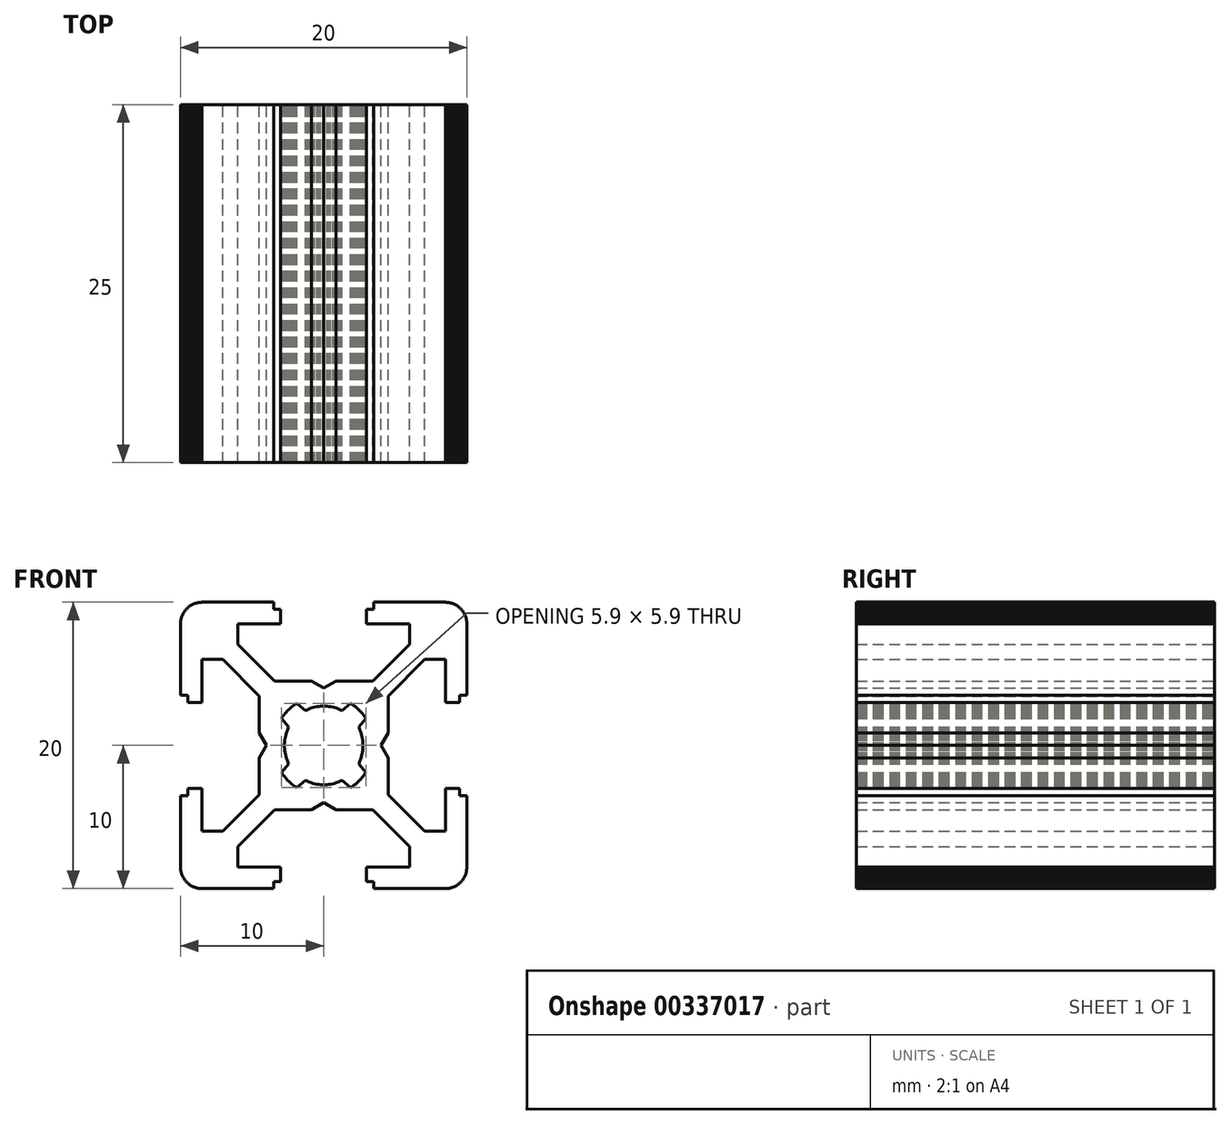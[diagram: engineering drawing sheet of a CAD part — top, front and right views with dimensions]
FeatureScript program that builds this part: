
annotation { "Feature Type Name" : "Feature", "Feature Type Description" : "" }
export const myFeature = defineFeature(function(context is Context, id is Id, definition is map)
    precondition{}
    {
        {
            var Q0;
            Q0=qCreatedBy(makeId("Front.planeOp"),FACE);
            var sketch = newSketch(context, id + "F0", { "sketchPlane" : qUnion([Q0])});
            skLineSegment(sketch, "E0", {"start": v(-10, -8.57) * mm, "end": v(-10, -8.5) * mm});
            skLineSegment(sketch, "E1", {"start": v(10, 8.5) * mm, "end": v(10, 8.57) * mm});
            skLineSegment(sketch, "E2", {"start": v(-2.74, -0.2) * mm, "end": v(-2.75, -0.07) * mm});
            skLineSegment(sketch, "E3", {"start": v(2.75, 0.07) * mm, "end": v(2.74, 0.2) * mm});
            skLineSegment(sketch, "E4", {"start": v(-10, -8.63) * mm, "end": v(-10, -8.57) * mm});
            skLineSegment(sketch, "E5", {"start": v(10, 8.57) * mm, "end": v(10, 8.63) * mm});
            skLineSegment(sketch, "E6", {"start": v(-2.73, -0.35) * mm, "end": v(-2.74, -0.2) * mm});
            skLineSegment(sketch, "E7", {"start": v(2.74, 0.2) * mm, "end": v(2.73, 0.35) * mm});
            skLineSegment(sketch, "E8", {"start": v(-9.99, -8.7) * mm, "end": v(-10, -8.63) * mm});
            skLineSegment(sketch, "E9", {"start": v(10, 8.63) * mm, "end": v(9.99, 8.7) * mm});
            skLineSegment(sketch, "E10", {"start": v(-2.7, -0.49) * mm, "end": v(-2.73, -0.35) * mm});
            skLineSegment(sketch, "E11", {"start": v(2.73, 0.35) * mm, "end": v(2.7, 0.49) * mm});
            skLineSegment(sketch, "E12", {"start": v(-9.98, -8.77) * mm, "end": v(-9.99, -8.7) * mm});
            skLineSegment(sketch, "E13", {"start": v(9.99, 8.7) * mm, "end": v(9.98, 8.77) * mm});
            skLineSegment(sketch, "E14", {"start": v(-9.96, -8.83) * mm, "end": v(-9.98, -8.77) * mm});
            skLineSegment(sketch, "E15", {"start": v(9.98, 8.77) * mm, "end": v(9.96, 8.83) * mm});
            skLineSegment(sketch, "E16", {"start": v(-2.68, -0.62) * mm, "end": v(-2.7, -0.49) * mm});
            skLineSegment(sketch, "E17", {"start": v(2.7, 0.49) * mm, "end": v(2.68, 0.62) * mm});
            skLineSegment(sketch, "E18", {"start": v(-9.95, -8.9) * mm, "end": v(-9.96, -8.83) * mm});
            skLineSegment(sketch, "E19", {"start": v(9.96, 8.83) * mm, "end": v(9.95, 8.9) * mm});
            skLineSegment(sketch, "E20", {"start": v(-2.64, -0.76) * mm, "end": v(-2.68, -0.62) * mm});
            skLineSegment(sketch, "E21", {"start": v(2.68, 0.62) * mm, "end": v(2.64, 0.76) * mm});
            skLineSegment(sketch, "E22", {"start": v(-9.93, -8.96) * mm, "end": v(-9.95, -8.9) * mm});
            skLineSegment(sketch, "E23", {"start": v(9.95, 8.9) * mm, "end": v(9.93, 8.96) * mm});
            skLineSegment(sketch, "E24", {"start": v(-2.6, -0.9) * mm, "end": v(-2.64, -0.76) * mm});
            skLineSegment(sketch, "E25", {"start": v(2.64, 0.76) * mm, "end": v(2.6, 0.9) * mm});
            skLineSegment(sketch, "E26", {"start": v(-9.9, -9.03) * mm, "end": v(-9.93, -8.96) * mm});
            skLineSegment(sketch, "E27", {"start": v(9.93, 8.96) * mm, "end": v(9.9, 9.03) * mm});
            skLineSegment(sketch, "E28", {"start": v(-2.55, -1.02) * mm, "end": v(-2.6, -0.9) * mm});
            skLineSegment(sketch, "E29", {"start": v(2.6, 0.9) * mm, "end": v(2.55, 1.02) * mm});
            skLineSegment(sketch, "E30", {"start": v(-9.88, -9.09) * mm, "end": v(-9.9, -9.03) * mm});
            skLineSegment(sketch, "E31", {"start": v(9.9, 9.03) * mm, "end": v(9.88, 9.09) * mm});
            skLineSegment(sketch, "E32", {"start": v(-2.5, -1.15) * mm, "end": v(-2.55, -1.02) * mm});
            skLineSegment(sketch, "E33", {"start": v(2.55, 1.02) * mm, "end": v(2.5, 1.15) * mm});
            skLineSegment(sketch, "E34", {"start": v(-9.85, -9.15) * mm, "end": v(-9.88, -9.09) * mm});
            skLineSegment(sketch, "E35", {"start": v(9.88, 9.09) * mm, "end": v(9.85, 9.15) * mm});
            skLineSegment(sketch, "E36", {"start": v(-2.44, -1.28) * mm, "end": v(-2.5, -1.15) * mm});
            skLineSegment(sketch, "E37", {"start": v(2.5, 1.15) * mm, "end": v(2.44, 1.28) * mm});
            skLineSegment(sketch, "E38", {"start": v(-9.82, -9.21) * mm, "end": v(-9.85, -9.15) * mm});
            skLineSegment(sketch, "E39", {"start": v(9.85, 9.15) * mm, "end": v(9.82, 9.21) * mm});
            skLineSegment(sketch, "E40", {"start": v(-9.79, -9.27) * mm, "end": v(-9.82, -9.21) * mm});
            skLineSegment(sketch, "E41", {"start": v(9.82, 9.21) * mm, "end": v(9.79, 9.27) * mm});
            skLineSegment(sketch, "E42", {"start": v(4.5, -0.87) * mm, "end": v(4, 0) * mm});
            skLineSegment(sketch, "E43", {"start": v(-4, 0) * mm, "end": v(-4.5, 0.87) * mm});
            skLineSegment(sketch, "E44", {"start": v(-9.75, -9.33) * mm, "end": v(-9.79, -9.27) * mm});
            skLineSegment(sketch, "E45", {"start": v(9.79, 9.27) * mm, "end": v(9.75, 9.33) * mm});
            skLineSegment(sketch, "E46", {"start": v(-2.87, -2) * mm, "end": v(-2.95, -1.89) * mm});
            skLineSegment(sketch, "E47", {"start": v(2.95, 1.89) * mm, "end": v(2.87, 2) * mm});
            skLineSegment(sketch, "E48", {"start": v(-9.71, -9.38) * mm, "end": v(-9.75, -9.33) * mm});
            skLineSegment(sketch, "E49", {"start": v(9.75, 9.33) * mm, "end": v(9.71, 9.38) * mm});
            skLineSegment(sketch, "E50", {"start": v(-2.8, -2.11) * mm, "end": v(-2.87, -2) * mm});
            skLineSegment(sketch, "E51", {"start": v(2.87, 2) * mm, "end": v(2.8, 2.11) * mm});
            skLineSegment(sketch, "E52", {"start": v(-9.67, -9.44) * mm, "end": v(-9.71, -9.38) * mm});
            skLineSegment(sketch, "E53", {"start": v(9.71, 9.38) * mm, "end": v(9.67, 9.44) * mm});
            skLineSegment(sketch, "E54", {"start": v(-2.7, -2.22) * mm, "end": v(-2.8, -2.11) * mm});
            skLineSegment(sketch, "E55", {"start": v(2.8, 2.11) * mm, "end": v(2.7, 2.22) * mm});
            skLineSegment(sketch, "E56", {"start": v(-9.63, -9.49) * mm, "end": v(-9.67, -9.44) * mm});
            skLineSegment(sketch, "E57", {"start": v(9.67, 9.44) * mm, "end": v(9.63, 9.49) * mm});
            skLineSegment(sketch, "E58", {"start": v(2.95, -1.89) * mm, "end": v(2.44, -1.28) * mm});
            skLineSegment(sketch, "E59", {"start": v(-2.44, 1.28) * mm, "end": v(-2.95, 1.89) * mm});
            skLineSegment(sketch, "E60", {"start": v(-2.62, -2.32) * mm, "end": v(-2.7, -2.22) * mm});
            skLineSegment(sketch, "E61", {"start": v(2.7, 2.22) * mm, "end": v(2.62, 2.32) * mm});
            skLineSegment(sketch, "E62", {"start": v(-9.58, -9.54) * mm, "end": v(-9.63, -9.49) * mm});
            skLineSegment(sketch, "E63", {"start": v(9.63, 9.49) * mm, "end": v(9.58, 9.54) * mm});
            skLineSegment(sketch, "E64", {"start": v(-2.52, -2.43) * mm, "end": v(-2.62, -2.32) * mm});
            skLineSegment(sketch, "E65", {"start": v(2.62, 2.32) * mm, "end": v(2.52, 2.43) * mm});
            skLineSegment(sketch, "E66", {"start": v(-2.43, -2.52) * mm, "end": v(-2.52, -2.43) * mm});
            skLineSegment(sketch, "E67", {"start": v(2.52, 2.43) * mm, "end": v(2.43, 2.52) * mm});
            skLineSegment(sketch, "E68", {"start": v(-9.54, -9.58) * mm, "end": v(-9.58, -9.54) * mm});
            skLineSegment(sketch, "E69", {"start": v(7.06, -6) * mm, "end": v(4.5, -3.44) * mm});
            skLineSegment(sketch, "E70", {"start": v(-4.5, 3.44) * mm, "end": v(-7.06, 6) * mm});
            skLineSegment(sketch, "E71", {"start": v(6, -7.06) * mm, "end": v(3.44, -4.5) * mm});
            skLineSegment(sketch, "E72", {"start": v(-3.44, 4.5) * mm, "end": v(-6, 7.06) * mm});
            skLineSegment(sketch, "E73", {"start": v(9.58, 9.54) * mm, "end": v(9.54, 9.58) * mm});
            skLineSegment(sketch, "E74", {"start": v(-2.32, -2.62) * mm, "end": v(-2.43, -2.52) * mm});
            skLineSegment(sketch, "E75", {"start": v(2.43, 2.52) * mm, "end": v(2.32, 2.62) * mm});
            skLineSegment(sketch, "E76", {"start": v(-9.49, -9.63) * mm, "end": v(-9.54, -9.58) * mm});
            skLineSegment(sketch, "E77", {"start": v(9.54, 9.58) * mm, "end": v(9.49, 9.63) * mm});
            skLineSegment(sketch, "E78", {"start": v(-2.22, -2.7) * mm, "end": v(-2.32, -2.62) * mm});
            skLineSegment(sketch, "E79", {"start": v(2.32, 2.62) * mm, "end": v(2.22, 2.7) * mm});
            skLineSegment(sketch, "E80", {"start": v(1.89, -2.95) * mm, "end": v(1.28, -2.44) * mm});
            skLineSegment(sketch, "E81", {"start": v(-1.28, 2.44) * mm, "end": v(-1.89, 2.95) * mm});
            skLineSegment(sketch, "E82", {"start": v(-9.44, -9.67) * mm, "end": v(-9.49, -9.63) * mm});
            skLineSegment(sketch, "E83", {"start": v(9.49, 9.63) * mm, "end": v(9.44, 9.67) * mm});
            skLineSegment(sketch, "E84", {"start": v(-2.11, -2.8) * mm, "end": v(-2.22, -2.7) * mm});
            skLineSegment(sketch, "E85", {"start": v(2.22, 2.7) * mm, "end": v(2.11, 2.8) * mm});
            skLineSegment(sketch, "E86", {"start": v(-9.38, -9.71) * mm, "end": v(-9.44, -9.67) * mm});
            skLineSegment(sketch, "E87", {"start": v(9.44, 9.67) * mm, "end": v(9.38, 9.71) * mm});
            skLineSegment(sketch, "E88", {"start": v(-2, -2.87) * mm, "end": v(-2.11, -2.8) * mm});
            skLineSegment(sketch, "E89", {"start": v(2.11, 2.8) * mm, "end": v(2, 2.87) * mm});
            skLineSegment(sketch, "E90", {"start": v(-9.33, -9.75) * mm, "end": v(-9.38, -9.71) * mm});
            skLineSegment(sketch, "E91", {"start": v(9.38, 9.71) * mm, "end": v(9.33, 9.75) * mm});
            skLineSegment(sketch, "E92", {"start": v(-1.89, -2.95) * mm, "end": v(-2, -2.87) * mm});
            skLineSegment(sketch, "E93", {"start": v(2, 2.87) * mm, "end": v(1.89, 2.95) * mm});
            skLineSegment(sketch, "E94", {"start": v(-9.27, -9.79) * mm, "end": v(-9.33, -9.75) * mm});
            skLineSegment(sketch, "E95", {"start": v(9.33, 9.75) * mm, "end": v(9.27, 9.79) * mm});
            skLineSegment(sketch, "E96", {"start": v(0.87, -4.5) * mm, "end": v(0, -4) * mm});
            skLineSegment(sketch, "E97", {"start": v(0, 4) * mm, "end": v(-0.87, 4.5) * mm});
            skLineSegment(sketch, "E98", {"start": v(-9.21, -9.82) * mm, "end": v(-9.27, -9.79) * mm});
            skLineSegment(sketch, "E99", {"start": v(9.27, 9.79) * mm, "end": v(9.21, 9.82) * mm});
            skLineSegment(sketch, "E100", {"start": v(-9.15, -9.85) * mm, "end": v(-9.21, -9.82) * mm});
            skLineSegment(sketch, "E101", {"start": v(9.21, 9.82) * mm, "end": v(9.15, 9.85) * mm});
            skLineSegment(sketch, "E102", {"start": v(-1.15, -2.5) * mm, "end": v(-1.28, -2.44) * mm});
            skLineSegment(sketch, "E103", {"start": v(1.28, 2.44) * mm, "end": v(1.15, 2.5) * mm});
            skLineSegment(sketch, "E104", {"start": v(-9.09, -9.88) * mm, "end": v(-9.15, -9.85) * mm});
            skLineSegment(sketch, "E105", {"start": v(9.15, 9.85) * mm, "end": v(9.09, 9.88) * mm});
            skLineSegment(sketch, "E106", {"start": v(-1.02, -2.55) * mm, "end": v(-1.15, -2.5) * mm});
            skLineSegment(sketch, "E107", {"start": v(1.15, 2.5) * mm, "end": v(1.02, 2.55) * mm});
            skLineSegment(sketch, "E108", {"start": v(-9.03, -9.9) * mm, "end": v(-9.09, -9.88) * mm});
            skLineSegment(sketch, "E109", {"start": v(9.09, 9.88) * mm, "end": v(9.03, 9.9) * mm});
            skLineSegment(sketch, "E110", {"start": v(-0.9, -2.6) * mm, "end": v(-1.02, -2.55) * mm});
            skLineSegment(sketch, "E111", {"start": v(1.02, 2.55) * mm, "end": v(0.9, 2.6) * mm});
            skLineSegment(sketch, "E112", {"start": v(-8.96, -9.93) * mm, "end": v(-9.03, -9.9) * mm});
            skLineSegment(sketch, "E113", {"start": v(9.03, 9.9) * mm, "end": v(8.96, 9.93) * mm});
            skLineSegment(sketch, "E114", {"start": v(-0.76, -2.64) * mm, "end": v(-0.9, -2.6) * mm});
            skLineSegment(sketch, "E115", {"start": v(0.9, 2.6) * mm, "end": v(0.76, 2.64) * mm});
            skLineSegment(sketch, "E116", {"start": v(-8.9, -9.95) * mm, "end": v(-8.96, -9.93) * mm});
            skLineSegment(sketch, "E117", {"start": v(8.96, 9.93) * mm, "end": v(8.9, 9.95) * mm});
            skLineSegment(sketch, "E118", {"start": v(-0.62, -2.68) * mm, "end": v(-0.76, -2.64) * mm});
            skLineSegment(sketch, "E119", {"start": v(0.76, 2.64) * mm, "end": v(0.62, 2.68) * mm});
            skLineSegment(sketch, "E120", {"start": v(-8.83, -9.96) * mm, "end": v(-8.9, -9.95) * mm});
            skLineSegment(sketch, "E121", {"start": v(8.9, 9.95) * mm, "end": v(8.83, 9.96) * mm});
            skLineSegment(sketch, "E122", {"start": v(-0.49, -2.7) * mm, "end": v(-0.62, -2.68) * mm});
            skLineSegment(sketch, "E123", {"start": v(0.62, 2.68) * mm, "end": v(0.49, 2.7) * mm});
            skLineSegment(sketch, "E124", {"start": v(-8.77, -9.98) * mm, "end": v(-8.83, -9.96) * mm});
            skLineSegment(sketch, "E125", {"start": v(8.83, 9.96) * mm, "end": v(8.77, 9.98) * mm});
            skLineSegment(sketch, "E126", {"start": v(-8.7, -9.99) * mm, "end": v(-8.77, -9.98) * mm});
            skLineSegment(sketch, "E127", {"start": v(8.77, 9.98) * mm, "end": v(8.7, 9.99) * mm});
            skLineSegment(sketch, "E128", {"start": v(-0.35, -2.73) * mm, "end": v(-0.49, -2.7) * mm});
            skLineSegment(sketch, "E129", {"start": v(0.49, 2.7) * mm, "end": v(0.35, 2.73) * mm});
            skLineSegment(sketch, "E130", {"start": v(-8.63, -10) * mm, "end": v(-8.7, -9.99) * mm});
            skLineSegment(sketch, "E131", {"start": v(8.7, 9.99) * mm, "end": v(8.63, 10) * mm});
            skLineSegment(sketch, "E132", {"start": v(-0.2, -2.74) * mm, "end": v(-0.35, -2.73) * mm});
            skLineSegment(sketch, "E133", {"start": v(0.35, 2.73) * mm, "end": v(0.2, 2.74) * mm});
            skLineSegment(sketch, "E134", {"start": v(-8.57, -10) * mm, "end": v(-8.63, -10) * mm});
            skLineSegment(sketch, "E135", {"start": v(8.63, 10) * mm, "end": v(8.57, 10) * mm});
            skLineSegment(sketch, "E136", {"start": v(-0.07, -2.75) * mm, "end": v(-0.2, -2.74) * mm});
            skLineSegment(sketch, "E137", {"start": v(0.2, 2.74) * mm, "end": v(0.07, 2.75) * mm});
            skLineSegment(sketch, "E138", {"start": v(-8.5, -10) * mm, "end": v(-8.57, -10) * mm});
            skLineSegment(sketch, "E139", {"start": v(8.57, 10) * mm, "end": v(8.5, 10) * mm});
            skLineSegment(sketch, "E140", {"start": v(-8.5, -10) * mm, "end": v(-3.5, -10) * mm});
            skLineSegment(sketch, "E141", {"start": v(3.5, -10) * mm, "end": v(8.5, -10) * mm});
            skLineSegment(sketch, "E142", {"start": v(-3.5, -9.5) * mm, "end": v(-3, -9.5) * mm});
            skLineSegment(sketch, "E143", {"start": v(3, -9.5) * mm, "end": v(3.5, -9.5) * mm});
            skLineSegment(sketch, "E144", {"start": v(-6, -8.5) * mm, "end": v(-3, -8.5) * mm});
            skLineSegment(sketch, "E145", {"start": v(3, -8.5) * mm, "end": v(6, -8.5) * mm});
            skLineSegment(sketch, "E146", {"start": v(-8.5, -6) * mm, "end": v(-7.06, -6) * mm});
            skLineSegment(sketch, "E147", {"start": v(7.06, -6) * mm, "end": v(8.5, -6) * mm});
            skLineSegment(sketch, "E148", {"start": v(-3.44, -4.5) * mm, "end": v(-0.87, -4.5) * mm});
            skLineSegment(sketch, "E149", {"start": v(0.87, -4.5) * mm, "end": v(3.44, -4.5) * mm});
            skLineSegment(sketch, "E150", {"start": v(-10, -3.5) * mm, "end": v(-9.5, -3.5) * mm});
            skLineSegment(sketch, "E151", {"start": v(9.5, -3.5) * mm, "end": v(10, -3.5) * mm});
            skLineSegment(sketch, "E152", {"start": v(-9.5, -3) * mm, "end": v(-8.5, -3) * mm});
            skLineSegment(sketch, "E153", {"start": v(8.5, -3) * mm, "end": v(9.5, -3) * mm});
            skLineSegment(sketch, "E154", {"start": v(-0.07, -2.75) * mm, "end": v(0.07, -2.75) * mm});
            skLineSegment(sketch, "E155", {"start": v(-0.07, 2.75) * mm, "end": v(0.07, 2.75) * mm});
            skLineSegment(sketch, "E156", {"start": v(8.5, 3) * mm, "end": v(9.5, 3) * mm});
            skLineSegment(sketch, "E157", {"start": v(-9.5, 3) * mm, "end": v(-8.5, 3) * mm});
            skLineSegment(sketch, "E158", {"start": v(9.5, 3.5) * mm, "end": v(10, 3.5) * mm});
            skLineSegment(sketch, "E159", {"start": v(-10, 3.5) * mm, "end": v(-9.5, 3.5) * mm});
            skLineSegment(sketch, "E160", {"start": v(0.87, 4.5) * mm, "end": v(3.44, 4.5) * mm});
            skLineSegment(sketch, "E161", {"start": v(-3.44, 4.5) * mm, "end": v(-0.87, 4.5) * mm});
            skLineSegment(sketch, "E162", {"start": v(7.06, 6) * mm, "end": v(8.5, 6) * mm});
            skLineSegment(sketch, "E163", {"start": v(-8.5, 6) * mm, "end": v(-7.06, 6) * mm});
            skLineSegment(sketch, "E164", {"start": v(3, 8.5) * mm, "end": v(6, 8.5) * mm});
            skLineSegment(sketch, "E165", {"start": v(-6, 8.5) * mm, "end": v(-3, 8.5) * mm});
            skLineSegment(sketch, "E166", {"start": v(3, 9.5) * mm, "end": v(3.5, 9.5) * mm});
            skLineSegment(sketch, "E167", {"start": v(-3.5, 9.5) * mm, "end": v(-3, 9.5) * mm});
            skLineSegment(sketch, "E168", {"start": v(3.5, 10) * mm, "end": v(8.5, 10) * mm});
            skLineSegment(sketch, "E169", {"start": v(-8.5, 10) * mm, "end": v(-3.5, 10) * mm});
            skLineSegment(sketch, "E170", {"start": v(8.5, -10) * mm, "end": v(8.57, -10) * mm});
            skLineSegment(sketch, "E171", {"start": v(-8.57, 10) * mm, "end": v(-8.5, 10) * mm});
            skLineSegment(sketch, "E172", {"start": v(0.07, -2.75) * mm, "end": v(0.2, -2.74) * mm});
            skLineSegment(sketch, "E173", {"start": v(-0.2, 2.74) * mm, "end": v(-0.07, 2.75) * mm});
            skLineSegment(sketch, "E174", {"start": v(8.57, -10) * mm, "end": v(8.63, -10) * mm});
            skLineSegment(sketch, "E175", {"start": v(-8.63, 10) * mm, "end": v(-8.57, 10) * mm});
            skLineSegment(sketch, "E176", {"start": v(0.2, -2.74) * mm, "end": v(0.35, -2.73) * mm});
            skLineSegment(sketch, "E177", {"start": v(-0.35, 2.73) * mm, "end": v(-0.2, 2.74) * mm});
            skLineSegment(sketch, "E178", {"start": v(8.63, -10) * mm, "end": v(8.7, -9.99) * mm});
            skLineSegment(sketch, "E179", {"start": v(-8.7, 9.99) * mm, "end": v(-8.63, 10) * mm});
            skLineSegment(sketch, "E180", {"start": v(0.35, -2.73) * mm, "end": v(0.49, -2.7) * mm});
            skLineSegment(sketch, "E181", {"start": v(-0.49, 2.7) * mm, "end": v(-0.35, 2.73) * mm});
            skLineSegment(sketch, "E182", {"start": v(8.7, -9.99) * mm, "end": v(8.77, -9.98) * mm});
            skLineSegment(sketch, "E183", {"start": v(-8.77, 9.98) * mm, "end": v(-8.7, 9.99) * mm});
            skLineSegment(sketch, "E184", {"start": v(8.77, -9.98) * mm, "end": v(8.83, -9.96) * mm});
            skLineSegment(sketch, "E185", {"start": v(-8.83, 9.96) * mm, "end": v(-8.77, 9.98) * mm});
            skLineSegment(sketch, "E186", {"start": v(0.49, -2.7) * mm, "end": v(0.62, -2.68) * mm});
            skLineSegment(sketch, "E187", {"start": v(-0.62, 2.68) * mm, "end": v(-0.49, 2.7) * mm});
            skLineSegment(sketch, "E188", {"start": v(8.83, -9.96) * mm, "end": v(8.9, -9.95) * mm});
            skLineSegment(sketch, "E189", {"start": v(-8.9, 9.95) * mm, "end": v(-8.83, 9.96) * mm});
            skLineSegment(sketch, "E190", {"start": v(0.62, -2.68) * mm, "end": v(0.76, -2.64) * mm});
            skLineSegment(sketch, "E191", {"start": v(-0.76, 2.64) * mm, "end": v(-0.62, 2.68) * mm});
            skLineSegment(sketch, "E192", {"start": v(8.9, -9.95) * mm, "end": v(8.96, -9.93) * mm});
            skLineSegment(sketch, "E193", {"start": v(-8.96, 9.93) * mm, "end": v(-8.9, 9.95) * mm});
            skLineSegment(sketch, "E194", {"start": v(0.76, -2.64) * mm, "end": v(0.9, -2.6) * mm});
            skLineSegment(sketch, "E195", {"start": v(-0.9, 2.6) * mm, "end": v(-0.76, 2.64) * mm});
            skLineSegment(sketch, "E196", {"start": v(8.96, -9.93) * mm, "end": v(9.03, -9.9) * mm});
            skLineSegment(sketch, "E197", {"start": v(-9.03, 9.9) * mm, "end": v(-8.96, 9.93) * mm});
            skLineSegment(sketch, "E198", {"start": v(0.9, -2.6) * mm, "end": v(1.02, -2.55) * mm});
            skLineSegment(sketch, "E199", {"start": v(-1.02, 2.55) * mm, "end": v(-0.9, 2.6) * mm});
            skLineSegment(sketch, "E200", {"start": v(9.03, -9.9) * mm, "end": v(9.09, -9.88) * mm});
            skLineSegment(sketch, "E201", {"start": v(-9.09, 9.88) * mm, "end": v(-9.03, 9.9) * mm});
            skLineSegment(sketch, "E202", {"start": v(1.02, -2.55) * mm, "end": v(1.15, -2.5) * mm});
            skLineSegment(sketch, "E203", {"start": v(-1.15, 2.5) * mm, "end": v(-1.02, 2.55) * mm});
            skLineSegment(sketch, "E204", {"start": v(9.09, -9.88) * mm, "end": v(9.15, -9.85) * mm});
            skLineSegment(sketch, "E205", {"start": v(-9.15, 9.85) * mm, "end": v(-9.09, 9.88) * mm});
            skLineSegment(sketch, "E206", {"start": v(1.15, -2.5) * mm, "end": v(1.28, -2.44) * mm});
            skLineSegment(sketch, "E207", {"start": v(-1.28, 2.44) * mm, "end": v(-1.15, 2.5) * mm});
            skLineSegment(sketch, "E208", {"start": v(9.15, -9.85) * mm, "end": v(9.21, -9.82) * mm});
            skLineSegment(sketch, "E209", {"start": v(-9.21, 9.82) * mm, "end": v(-9.15, 9.85) * mm});
            skLineSegment(sketch, "E210", {"start": v(9.21, -9.82) * mm, "end": v(9.27, -9.79) * mm});
            skLineSegment(sketch, "E211", {"start": v(-9.27, 9.79) * mm, "end": v(-9.21, 9.82) * mm});
            skLineSegment(sketch, "E212", {"start": v(-0.87, -4.5) * mm, "end": v(0, -4) * mm});
            skLineSegment(sketch, "E213", {"start": v(0, 4) * mm, "end": v(0.87, 4.5) * mm});
            skLineSegment(sketch, "E214", {"start": v(9.27, -9.79) * mm, "end": v(9.33, -9.75) * mm});
            skLineSegment(sketch, "E215", {"start": v(-9.33, 9.75) * mm, "end": v(-9.27, 9.79) * mm});
            skLineSegment(sketch, "E216", {"start": v(1.89, -2.95) * mm, "end": v(2, -2.87) * mm});
            skLineSegment(sketch, "E217", {"start": v(-2, 2.87) * mm, "end": v(-1.89, 2.95) * mm});
            skLineSegment(sketch, "E218", {"start": v(9.33, -9.75) * mm, "end": v(9.38, -9.71) * mm});
            skLineSegment(sketch, "E219", {"start": v(-9.38, 9.71) * mm, "end": v(-9.33, 9.75) * mm});
            skLineSegment(sketch, "E220", {"start": v(2, -2.87) * mm, "end": v(2.11, -2.8) * mm});
            skLineSegment(sketch, "E221", {"start": v(-2.11, 2.8) * mm, "end": v(-2, 2.87) * mm});
            skLineSegment(sketch, "E222", {"start": v(9.38, -9.71) * mm, "end": v(9.44, -9.67) * mm});
            skLineSegment(sketch, "E223", {"start": v(-9.44, 9.67) * mm, "end": v(-9.38, 9.71) * mm});
            skLineSegment(sketch, "E224", {"start": v(2.11, -2.8) * mm, "end": v(2.22, -2.7) * mm});
            skLineSegment(sketch, "E225", {"start": v(-2.22, 2.7) * mm, "end": v(-2.11, 2.8) * mm});
            skLineSegment(sketch, "E226", {"start": v(9.44, -9.67) * mm, "end": v(9.49, -9.63) * mm});
            skLineSegment(sketch, "E227", {"start": v(-9.49, 9.63) * mm, "end": v(-9.44, 9.67) * mm});
            skLineSegment(sketch, "E228", {"start": v(-1.89, -2.95) * mm, "end": v(-1.28, -2.44) * mm});
            skLineSegment(sketch, "E229", {"start": v(1.28, 2.44) * mm, "end": v(1.89, 2.95) * mm});
            skLineSegment(sketch, "E230", {"start": v(2.22, -2.7) * mm, "end": v(2.32, -2.62) * mm});
            skLineSegment(sketch, "E231", {"start": v(-2.32, 2.62) * mm, "end": v(-2.22, 2.7) * mm});
            skLineSegment(sketch, "E232", {"start": v(9.49, -9.63) * mm, "end": v(9.54, -9.58) * mm});
            skLineSegment(sketch, "E233", {"start": v(-9.54, 9.58) * mm, "end": v(-9.49, 9.63) * mm});
            skLineSegment(sketch, "E234", {"start": v(2.32, -2.62) * mm, "end": v(2.43, -2.52) * mm});
            skLineSegment(sketch, "E235", {"start": v(-2.43, 2.52) * mm, "end": v(-2.32, 2.62) * mm});
            skLineSegment(sketch, "E236", {"start": v(9.54, -9.58) * mm, "end": v(9.58, -9.54) * mm});
            skLineSegment(sketch, "E237", {"start": v(-7.06, -6) * mm, "end": v(-4.5, -3.44) * mm});
            skLineSegment(sketch, "E238", {"start": v(4.5, 3.44) * mm, "end": v(7.06, 6) * mm});
            skLineSegment(sketch, "E239", {"start": v(-6, -7.06) * mm, "end": v(-3.44, -4.5) * mm});
            skLineSegment(sketch, "E240", {"start": v(3.44, 4.5) * mm, "end": v(6, 7.06) * mm});
            skLineSegment(sketch, "E241", {"start": v(-9.58, 9.54) * mm, "end": v(-9.54, 9.58) * mm});
            skLineSegment(sketch, "E242", {"start": v(2.43, -2.52) * mm, "end": v(2.52, -2.43) * mm});
            skLineSegment(sketch, "E243", {"start": v(-2.52, 2.43) * mm, "end": v(-2.43, 2.52) * mm});
            skLineSegment(sketch, "E244", {"start": v(2.52, -2.43) * mm, "end": v(2.62, -2.32) * mm});
            skLineSegment(sketch, "E245", {"start": v(-2.62, 2.32) * mm, "end": v(-2.52, 2.43) * mm});
            skLineSegment(sketch, "E246", {"start": v(9.58, -9.54) * mm, "end": v(9.63, -9.49) * mm});
            skLineSegment(sketch, "E247", {"start": v(-9.63, 9.49) * mm, "end": v(-9.58, 9.54) * mm});
            skLineSegment(sketch, "E248", {"start": v(2.62, -2.32) * mm, "end": v(2.7, -2.22) * mm});
            skLineSegment(sketch, "E249", {"start": v(-2.7, 2.22) * mm, "end": v(-2.62, 2.32) * mm});
            skLineSegment(sketch, "E250", {"start": v(-2.95, -1.89) * mm, "end": v(-2.44, -1.28) * mm});
            skLineSegment(sketch, "E251", {"start": v(2.44, 1.28) * mm, "end": v(2.95, 1.89) * mm});
            skLineSegment(sketch, "E252", {"start": v(9.63, -9.49) * mm, "end": v(9.67, -9.44) * mm});
            skLineSegment(sketch, "E253", {"start": v(-9.67, 9.44) * mm, "end": v(-9.63, 9.49) * mm});
            skLineSegment(sketch, "E254", {"start": v(2.7, -2.22) * mm, "end": v(2.8, -2.11) * mm});
            skLineSegment(sketch, "E255", {"start": v(-2.8, 2.11) * mm, "end": v(-2.7, 2.22) * mm});
            skLineSegment(sketch, "E256", {"start": v(9.67, -9.44) * mm, "end": v(9.71, -9.38) * mm});
            skLineSegment(sketch, "E257", {"start": v(-9.71, 9.38) * mm, "end": v(-9.67, 9.44) * mm});
            skLineSegment(sketch, "E258", {"start": v(2.8, -2.11) * mm, "end": v(2.87, -2) * mm});
            skLineSegment(sketch, "E259", {"start": v(-2.87, 2) * mm, "end": v(-2.8, 2.11) * mm});
            skLineSegment(sketch, "E260", {"start": v(9.71, -9.38) * mm, "end": v(9.75, -9.33) * mm});
            skLineSegment(sketch, "E261", {"start": v(-9.75, 9.33) * mm, "end": v(-9.71, 9.38) * mm});
            skLineSegment(sketch, "E262", {"start": v(2.87, -2) * mm, "end": v(2.95, -1.89) * mm});
            skLineSegment(sketch, "E263", {"start": v(-2.95, 1.89) * mm, "end": v(-2.87, 2) * mm});
            skLineSegment(sketch, "E264", {"start": v(9.75, -9.33) * mm, "end": v(9.79, -9.27) * mm});
            skLineSegment(sketch, "E265", {"start": v(-9.79, 9.27) * mm, "end": v(-9.75, 9.33) * mm});
            skLineSegment(sketch, "E266", {"start": v(-4.5, -0.87) * mm, "end": v(-4, 0) * mm});
            skLineSegment(sketch, "E267", {"start": v(4, 0) * mm, "end": v(4.5, 0.87) * mm});
            skLineSegment(sketch, "E268", {"start": v(9.79, -9.27) * mm, "end": v(9.82, -9.21) * mm});
            skLineSegment(sketch, "E269", {"start": v(-9.82, 9.21) * mm, "end": v(-9.79, 9.27) * mm});
            skLineSegment(sketch, "E270", {"start": v(9.82, -9.21) * mm, "end": v(9.85, -9.15) * mm});
            skLineSegment(sketch, "E271", {"start": v(-9.85, 9.15) * mm, "end": v(-9.82, 9.21) * mm});
            skLineSegment(sketch, "E272", {"start": v(2.44, -1.28) * mm, "end": v(2.5, -1.15) * mm});
            skLineSegment(sketch, "E273", {"start": v(-2.5, 1.15) * mm, "end": v(-2.44, 1.28) * mm});
            skLineSegment(sketch, "E274", {"start": v(9.85, -9.15) * mm, "end": v(9.88, -9.09) * mm});
            skLineSegment(sketch, "E275", {"start": v(-9.88, 9.09) * mm, "end": v(-9.85, 9.15) * mm});
            skLineSegment(sketch, "E276", {"start": v(2.5, -1.15) * mm, "end": v(2.55, -1.02) * mm});
            skLineSegment(sketch, "E277", {"start": v(-2.55, 1.02) * mm, "end": v(-2.5, 1.15) * mm});
            skLineSegment(sketch, "E278", {"start": v(9.88, -9.09) * mm, "end": v(9.9, -9.03) * mm});
            skLineSegment(sketch, "E279", {"start": v(-9.9, 9.03) * mm, "end": v(-9.88, 9.09) * mm});
            skLineSegment(sketch, "E280", {"start": v(2.55, -1.02) * mm, "end": v(2.6, -0.9) * mm});
            skLineSegment(sketch, "E281", {"start": v(-2.6, 0.9) * mm, "end": v(-2.55, 1.02) * mm});
            skLineSegment(sketch, "E282", {"start": v(9.9, -9.03) * mm, "end": v(9.93, -8.96) * mm});
            skLineSegment(sketch, "E283", {"start": v(-9.93, 8.96) * mm, "end": v(-9.9, 9.03) * mm});
            skLineSegment(sketch, "E284", {"start": v(2.6, -0.9) * mm, "end": v(2.64, -0.76) * mm});
            skLineSegment(sketch, "E285", {"start": v(-2.64, 0.76) * mm, "end": v(-2.6, 0.9) * mm});
            skLineSegment(sketch, "E286", {"start": v(9.93, -8.96) * mm, "end": v(9.95, -8.9) * mm});
            skLineSegment(sketch, "E287", {"start": v(-9.95, 8.9) * mm, "end": v(-9.93, 8.96) * mm});
            skLineSegment(sketch, "E288", {"start": v(2.64, -0.76) * mm, "end": v(2.68, -0.62) * mm});
            skLineSegment(sketch, "E289", {"start": v(-2.68, 0.62) * mm, "end": v(-2.64, 0.76) * mm});
            skLineSegment(sketch, "E290", {"start": v(9.95, -8.9) * mm, "end": v(9.96, -8.83) * mm});
            skLineSegment(sketch, "E291", {"start": v(-9.96, 8.83) * mm, "end": v(-9.95, 8.9) * mm});
            skLineSegment(sketch, "E292", {"start": v(2.68, -0.62) * mm, "end": v(2.7, -0.49) * mm});
            skLineSegment(sketch, "E293", {"start": v(-2.7, 0.49) * mm, "end": v(-2.68, 0.62) * mm});
            skLineSegment(sketch, "E294", {"start": v(9.96, -8.83) * mm, "end": v(9.98, -8.77) * mm});
            skLineSegment(sketch, "E295", {"start": v(-9.98, 8.77) * mm, "end": v(-9.96, 8.83) * mm});
            skLineSegment(sketch, "E296", {"start": v(9.98, -8.77) * mm, "end": v(9.99, -8.7) * mm});
            skLineSegment(sketch, "E297", {"start": v(-9.99, 8.7) * mm, "end": v(-9.98, 8.77) * mm});
            skLineSegment(sketch, "E298", {"start": v(2.7, -0.49) * mm, "end": v(2.73, -0.35) * mm});
            skLineSegment(sketch, "E299", {"start": v(-2.73, 0.35) * mm, "end": v(-2.7, 0.49) * mm});
            skLineSegment(sketch, "E300", {"start": v(9.99, -8.7) * mm, "end": v(10, -8.63) * mm});
            skLineSegment(sketch, "E301", {"start": v(-10, 8.63) * mm, "end": v(-9.99, 8.7) * mm});
            skLineSegment(sketch, "E302", {"start": v(2.73, -0.35) * mm, "end": v(2.74, -0.2) * mm});
            skLineSegment(sketch, "E303", {"start": v(-2.74, 0.2) * mm, "end": v(-2.73, 0.35) * mm});
            skLineSegment(sketch, "E304", {"start": v(10, -8.63) * mm, "end": v(10, -8.57) * mm});
            skLineSegment(sketch, "E305", {"start": v(-10, 8.57) * mm, "end": v(-10, 8.63) * mm});
            skLineSegment(sketch, "E306", {"start": v(2.74, -0.2) * mm, "end": v(2.75, -0.07) * mm});
            skLineSegment(sketch, "E307", {"start": v(-2.75, 0.07) * mm, "end": v(-2.74, 0.2) * mm});
            skLineSegment(sketch, "E308", {"start": v(10, -8.57) * mm, "end": v(10, -8.5) * mm});
            skLineSegment(sketch, "E309", {"start": v(-10, 8.5) * mm, "end": v(-10, 8.57) * mm});
            skLineSegment(sketch, "E310", {"start": v(-10, 3.5) * mm, "end": v(-10, 8.5) * mm});
            skLineSegment(sketch, "E311", {"start": v(-10, -8.5) * mm, "end": v(-10, -3.5) * mm});
            skLineSegment(sketch, "E312", {"start": v(-9.5, 3) * mm, "end": v(-9.5, 3.5) * mm});
            skLineSegment(sketch, "E313", {"start": v(-9.5, -3.5) * mm, "end": v(-9.5, -3) * mm});
            skLineSegment(sketch, "E314", {"start": v(-8.5, 3) * mm, "end": v(-8.5, 6) * mm});
            skLineSegment(sketch, "E315", {"start": v(-8.5, -6) * mm, "end": v(-8.5, -3) * mm});
            skLineSegment(sketch, "E316", {"start": v(-6, 7.06) * mm, "end": v(-6, 8.5) * mm});
            skLineSegment(sketch, "E317", {"start": v(-6, -8.5) * mm, "end": v(-6, -7.06) * mm});
            skLineSegment(sketch, "E318", {"start": v(-4.5, 0.87) * mm, "end": v(-4.5, 3.44) * mm});
            skLineSegment(sketch, "E319", {"start": v(-4.5, -3.44) * mm, "end": v(-4.5, -0.87) * mm});
            skLineSegment(sketch, "E320", {"start": v(-3.5, 9.5) * mm, "end": v(-3.5, 10) * mm});
            skLineSegment(sketch, "E321", {"start": v(-3.5, -10) * mm, "end": v(-3.5, -9.5) * mm});
            skLineSegment(sketch, "E322", {"start": v(-3, 8.5) * mm, "end": v(-3, 9.5) * mm});
            skLineSegment(sketch, "E323", {"start": v(-3, -9.5) * mm, "end": v(-3, -8.5) * mm});
            skLineSegment(sketch, "E324", {"start": v(-2.75, -0.07) * mm, "end": v(-2.75, 0.07) * mm});
            skLineSegment(sketch, "E325", {"start": v(2.75, -0.07) * mm, "end": v(2.75, 0.07) * mm});
            skLineSegment(sketch, "E326", {"start": v(3, 8.5) * mm, "end": v(3, 9.5) * mm});
            skLineSegment(sketch, "E327", {"start": v(3, -9.5) * mm, "end": v(3, -8.5) * mm});
            skLineSegment(sketch, "E328", {"start": v(3.5, 9.5) * mm, "end": v(3.5, 10) * mm});
            skLineSegment(sketch, "E329", {"start": v(3.5, -10) * mm, "end": v(3.5, -9.5) * mm});
            skLineSegment(sketch, "E330", {"start": v(4.5, -3.44) * mm, "end": v(4.5, -0.87) * mm});
            skLineSegment(sketch, "E331", {"start": v(4.5, 0.87) * mm, "end": v(4.5, 3.44) * mm});
            skLineSegment(sketch, "E332", {"start": v(6, 7.06) * mm, "end": v(6, 8.5) * mm});
            skLineSegment(sketch, "E333", {"start": v(6, -8.5) * mm, "end": v(6, -7.06) * mm});
            skLineSegment(sketch, "E334", {"start": v(8.5, 3) * mm, "end": v(8.5, 6) * mm});
            skLineSegment(sketch, "E335", {"start": v(8.5, -6) * mm, "end": v(8.5, -3) * mm});
            skLineSegment(sketch, "E336", {"start": v(9.5, 3) * mm, "end": v(9.5, 3.5) * mm});
            skLineSegment(sketch, "E337", {"start": v(9.5, -3.5) * mm, "end": v(9.5, -3) * mm});
            skLineSegment(sketch, "E338", {"start": v(10, 3.5) * mm, "end": v(10, 8.5) * mm});
            skLineSegment(sketch, "E339", {"start": v(10, -8.5) * mm, "end": v(10, -3.5) * mm});
            skSolve(sketch);
        }
        {
            var Q0;
            Q0=makeQuery(id+"F0.imprint","IMPRINT",FACE,{"disambiguationData":[TD([[makeQuery(id+"F0.imprint","IMPRINT",EDGE,{"derivedFrom":sQuery(id+"F0.wireOp",EDGE,"E0")}),-1.0]])]});
            extrude(context, id + "F1", {"entities" : qUnion([Q0]), "depth" : 25 * mm});
        }
    });
